# Revit family: Lighting_Fixture-Edge_Lighting-Plaza_Large_LED
name_source: partatom
category: Lighting Fixtures
revit_build: Autodesk Revit Architecture 2014 (Build: 20131024_2115(x64)
units: mm (PartAtom-declared; Revit-internal decimal feet)

## types (1)
- Plaza - Large - 27K
    Apparent Load = 0 VA
    Catalog and Price List = http://www.edgelighting.com
    Color Filter = 16777215
    Content Version = A1.0
    Default Elevation = 4' - 0"
    Depth = 0' - 2 1/8"
    Description = Direct Wall Mount
    Dimming Compatibility Chart = http://www.edgelighting.com
    Dimming Lamp Color Temperature Shift = <None>
    Emit Shape Visible in Rendering = No
    Emit from Rectangle Length = 2' - 10"
    Emit from Rectangle Width = 1' - 10 1/8"
    Finish = Glass - Edge Lighting - M - Mirror
    Frequency = 60 Hz
    Height = 3' - 3 3/8"
    Installation and Service URL = See Product Page URL
    Lamp = 1991 lumens, very warm white 2700K 92+CRI LEDs.
    Lens Finish = Plastic - Edge Lighting - LED Lens
    Manufacturer = Edge Lighting
    Model = PLAZA
    Number of Poles = 1
    Phase = 1
    Photometric Web File = PLAZA-L-LED-27K.ies
    Power Factor = 1
    Product Documentation Link = http://www.edgelighting.com
    Product Name = Plaza Large LED
    Product Page URL = http://www.edgelighting.com
    Tilt Angle = 0.00°
    URL = http://www.edgelighting.com
    Video Link = https://www.youtube.com
    Voltage = 120 V
    Wattage Comments = LED lamps consume 103 watts; 115 total watts
    Width = 2' - 3 1/2"

## geometry (parser evidence)
native form markers: Blend x14, Sweep x1
no freeform markers — native parametric forms only
